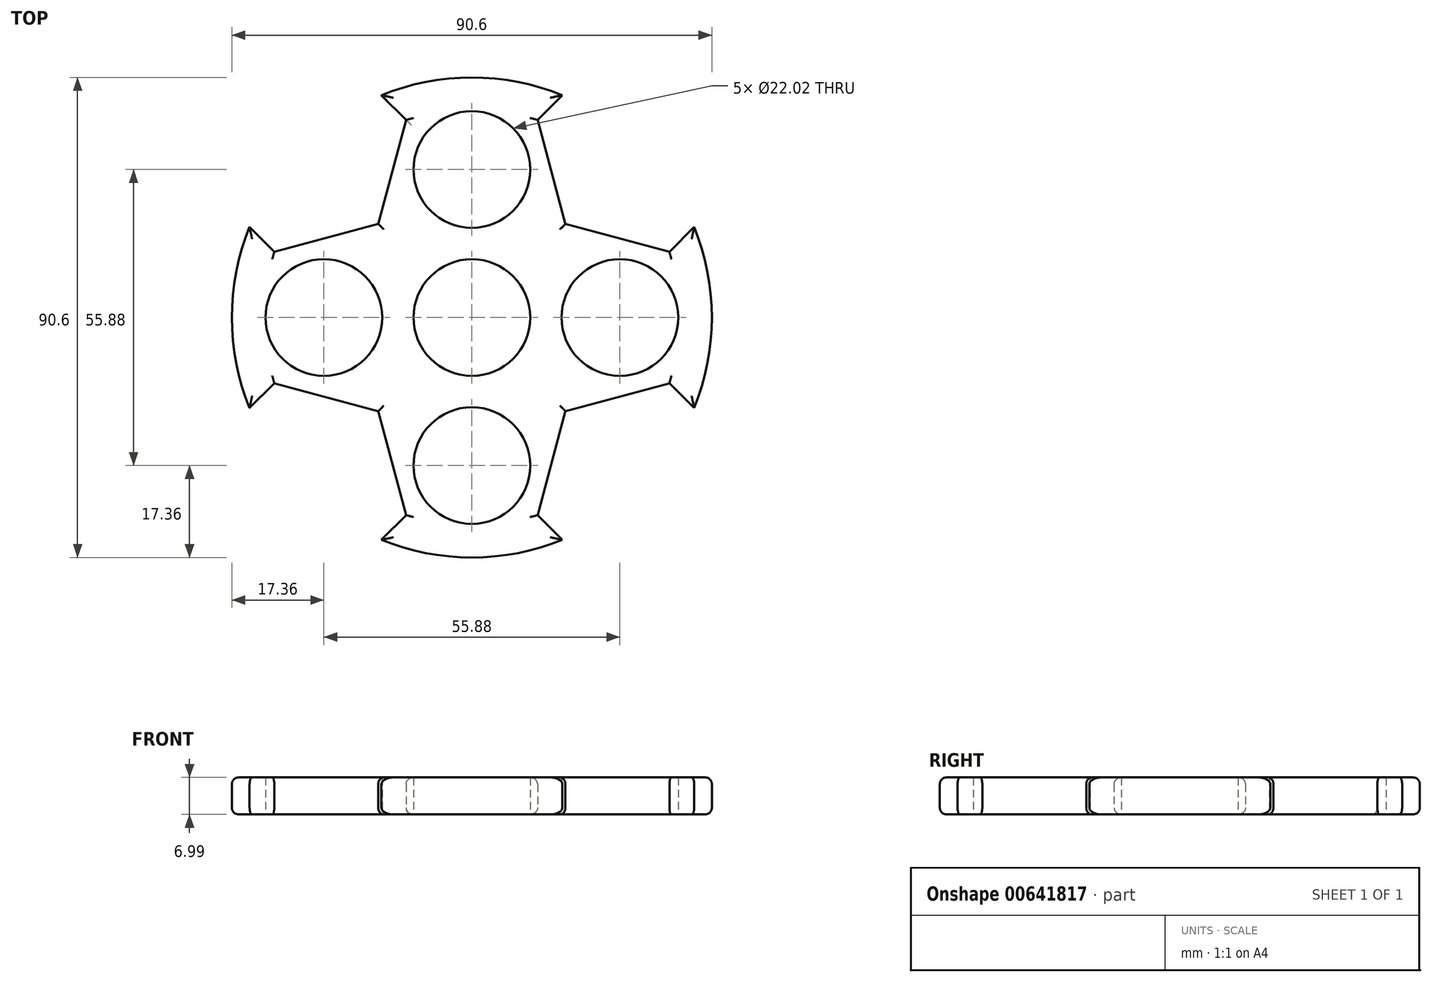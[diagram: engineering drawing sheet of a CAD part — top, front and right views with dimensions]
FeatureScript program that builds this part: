
annotation { "Feature Type Name" : "Feature", "Feature Type Description" : "" }
export const myFeature = defineFeature(function(context is Context, id is Id, definition is map)
    precondition{}
    {
        {
            var Q0;
            Q0=qCreatedBy(makeId("Top.planeOp"),FACE);
            var sketch = newSketch(context, id + "F0", { "sketchPlane" : qUnion([Q0])});
            skCircle(sketch, "E0", {"center": v(0, 0) * mm, "radius": 11.01 * mm});
            skCircle(sketch, "E1", {"center": v(0, 27.94) * mm, "radius": 11.01 * mm});
            skCircle(sketch, "E2", {"center": v(27.94, 0) * mm, "radius": 11.01 * mm});
            skLineSegment(sketch, "E3", {"start": v(0, 27.94) * mm, "end": v(0, 0) * mm});
            skLineSegment(sketch, "E4", {"start": v(27.94, 0) * mm, "end": v(0, 0) * mm});
            skCircle(sketch, "E5", {"center": v(0, -27.94) * mm, "radius": 11.01 * mm});
            skCircle(sketch, "E6", {"center": v(-27.94, 0) * mm, "radius": 11.01 * mm});
            skLineSegment(sketch, "E7", {"start": v(0, 0) * mm, "end": v(0, -27.94) * mm});
            skLineSegment(sketch, "E8", {"start": v(0, 0) * mm, "end": v(-27.94, 0) * mm});
            skCircle(sketch, "E9", {"center": v(0, 0) * mm, "radius": 45.3 * mm});
            skCircle(sketch, "E10.cCircle", {"center": v(-32.03, 32.03) * mm, "radius": 20.32 * mm, "construction": true});
            skLineSegment(sketch, "E10.0", {"start": v(-17.66, 17.66) * mm, "end": v(-37.3, 12.4) * mm});
            skLineSegment(sketch, "E10.1", {"start": v(-37.3, 12.4) * mm, "end": v(-51.66, 26.77) * mm});
            skLineSegment(sketch, "E10.2", {"start": v(-51.66, 26.77) * mm, "end": v(-46.4, 46.4) * mm});
            skLineSegment(sketch, "E10.3", {"start": v(-46.4, 46.4) * mm, "end": v(-26.77, 51.66) * mm});
            skLineSegment(sketch, "E10.4", {"start": v(-26.77, 51.66) * mm, "end": v(-12.4, 37.3) * mm});
            skLineSegment(sketch, "E10.5", {"start": v(-12.4, 37.3) * mm, "end": v(-17.66, 17.66) * mm});
            skLineSegment(sketch, "E11", {"start": v(0, 0) * mm, "end": v(-32.03, 32.03) * mm});
            skLineSegment(sketch, "E12.1.0", {"start": v(-26.77, -51.66) * mm, "end": v(-46.4, -46.4) * mm});
            skLineSegment(sketch, "E12.1.1", {"start": v(-17.66, -17.66) * mm, "end": v(-12.4, -37.3) * mm});
            skLineSegment(sketch, "E12.1.2", {"start": v(-46.4, -46.4) * mm, "end": v(-51.66, -26.77) * mm});
            skLineSegment(sketch, "E12.1.3", {"start": v(-51.66, -26.77) * mm, "end": v(-37.3, -12.4) * mm});
            skLineSegment(sketch, "E12.1.4", {"start": v(-37.3, -12.4) * mm, "end": v(-17.66, -17.66) * mm});
            skCircle(sketch, "E12.1.5", {"center": v(-32.03, -32.03) * mm, "radius": 20.32 * mm, "construction": true});
            skLineSegment(sketch, "E12.1.6", {"start": v(-12.4, -37.3) * mm, "end": v(-26.77, -51.66) * mm});
            skLineSegment(sketch, "E12.2.0", {"start": v(51.66, -26.77) * mm, "end": v(46.4, -46.4) * mm});
            skLineSegment(sketch, "E12.2.1", {"start": v(17.66, -17.66) * mm, "end": v(37.3, -12.4) * mm});
            skLineSegment(sketch, "E12.2.2", {"start": v(46.4, -46.4) * mm, "end": v(26.77, -51.66) * mm});
            skLineSegment(sketch, "E12.2.3", {"start": v(26.77, -51.66) * mm, "end": v(12.4, -37.3) * mm});
            skLineSegment(sketch, "E12.2.4", {"start": v(12.4, -37.3) * mm, "end": v(17.66, -17.66) * mm});
            skCircle(sketch, "E12.2.5", {"center": v(32.03, -32.03) * mm, "radius": 20.32 * mm, "construction": true});
            skLineSegment(sketch, "E12.2.6", {"start": v(37.3, -12.4) * mm, "end": v(51.66, -26.77) * mm});
            skLineSegment(sketch, "E12.3.0", {"start": v(26.77, 51.66) * mm, "end": v(46.4, 46.4) * mm});
            skLineSegment(sketch, "E12.3.1", {"start": v(17.66, 17.66) * mm, "end": v(12.4, 37.3) * mm});
            skLineSegment(sketch, "E12.3.2", {"start": v(46.4, 46.4) * mm, "end": v(51.66, 26.77) * mm});
            skLineSegment(sketch, "E12.3.3", {"start": v(51.66, 26.77) * mm, "end": v(37.3, 12.4) * mm});
            skLineSegment(sketch, "E12.3.4", {"start": v(37.3, 12.4) * mm, "end": v(17.66, 17.66) * mm});
            skCircle(sketch, "E12.3.5", {"center": v(32.03, 32.03) * mm, "radius": 20.32 * mm, "construction": true});
            skLineSegment(sketch, "E12.3.6", {"start": v(12.4, 37.3) * mm, "end": v(26.77, 51.66) * mm});
            skLineSegment(sketch, "E13", {"start": v(-32.03, -32.03) * mm, "end": v(0, 0) * mm});
            skLineSegment(sketch, "E14", {"start": v(0, 0) * mm, "end": v(32.03, -32.03) * mm});
            skLineSegment(sketch, "E15", {"start": v(0, 0) * mm, "end": v(32.03, 32.03) * mm});
            skSolve(sketch);
        }
        {
            var Q0;
            Q0=makeQuery(id+"F0.imprint","IMPRINT",FACE,{"disambiguationData":[TD([[makeQuery(id+"F0.imprint","IMPRINT",EDGE,{"derivedFrom":sQuery(id+"F0.wireOp",EDGE,"E2")}),-1.0]])]});
            var Q1;
            Q1=makeQuery(id+"F0.imprint","IMPRINT",FACE,{"disambiguationData":[TD([[makeQuery(id+"F0.imprint","IMPRINT",EDGE,{"derivedFrom":sQuery(id+"F0.wireOp",EDGE,"E1")}),-1.0]])]});
            var Q2;
            Q2=makeQuery(id+"F0.imprint","IMPRINT",FACE,{"disambiguationData":[TD([[makeQuery(id+"F0.imprint","IMPRINT",EDGE,{"derivedFrom":sQuery(id+"F0.wireOp",EDGE,"E6")}),-1.0]])]});
            var Q3;
            Q3=makeQuery(id+"F0.imprint","IMPRINT",FACE,{"disambiguationData":[TD([[makeQuery(id+"F0.imprint","IMPRINT",EDGE,{"derivedFrom":sQuery(id+"F0.wireOp",EDGE,"E5")}),-1.0]])]});
            extrude(context, id + "F1", {"entities" : qUnion([Q0, Q1, Q2, Q3]), "depth" : 7 * mm, "offsetDistance" : 25.4 * mm});
        }
        {
            var Q0;
            Q0=makeQuery(id+"F1.opExtrude","CAP_EDGE",EDGE,{"disambiguationData":[OSD([sQuery(id+"F0.wireOp",EDGE,"E10.5")])],"isStart":false});
            var Q1;
            Q1=makeQuery(id+"F1.opExtrude","CAP_EDGE",EDGE,{"disambiguationData":[OSD([sQuery(id+"F0.wireOp",EDGE,"E10.4")])],"isStart":false});
            var Q2;
            {var subQ0=sQuery(id+"F0.wireOp",EDGE,"E9");Q2=makeQuery(id+"F1.opExtrude","CAP_EDGE",EDGE,{"disambiguationData":[OSD([subQ0]),TDD([makeQuery(id+"F0.imprint","IMPRINT",EDGE,{"disambiguationData":[TD([[makeQuery(id+"F0.imprint","INTERSECT",VERTEX,{"derivedFrom":[subQ0,sQuery(id+"F0.wireOp",EDGE,"E12.3.6")]}),-1.0]])],"derivedFrom":subQ0})])],"isStart":false});}
            var Q3;
            Q3=makeQuery(id+"F1.opExtrude","CAP_EDGE",EDGE,{"disambiguationData":[OSD([sQuery(id+"F0.wireOp",EDGE,"E12.3.6")])],"isStart":false});
            var Q4;
            Q4=makeQuery(id+"F1.opExtrude","CAP_EDGE",EDGE,{"disambiguationData":[OSD([sQuery(id+"F0.wireOp",EDGE,"E12.3.1")])],"isStart":false});
            var Q5;
            Q5=makeQuery(id+"F1.opExtrude","CAP_EDGE",EDGE,{"disambiguationData":[OSD([sQuery(id+"F0.wireOp",EDGE,"E12.3.4")])],"isStart":false});
            var Q6;
            Q6=makeQuery(id+"F1.opExtrude","CAP_EDGE",EDGE,{"disambiguationData":[OSD([sQuery(id+"F0.wireOp",EDGE,"E10.0")])],"isStart":false});
            var Q7;
            Q7=makeQuery(id+"F1.opExtrude","CAP_EDGE",EDGE,{"disambiguationData":[OSD([sQuery(id+"F0.wireOp",EDGE,"E10.1")])],"isStart":false});
            var Q8;
            Q8=makeQuery(id+"F1.opExtrude","CAP_EDGE",EDGE,{"disambiguationData":[OSD([sQuery(id+"F0.wireOp",EDGE,"E12.1.3")])],"isStart":false});
            var Q9;
            Q9=makeQuery(id+"F1.opExtrude","CAP_EDGE",EDGE,{"disambiguationData":[OSD([sQuery(id+"F0.wireOp",EDGE,"E12.1.4")])],"isStart":false});
            var Q10;
            {var subQ0=sQuery(id+"F0.wireOp",EDGE,"E9");Q10=makeQuery(id+"F1.opExtrude","CAP_EDGE",EDGE,{"disambiguationData":[OSD([subQ0]),TDD([makeQuery(id+"F0.imprint","IMPRINT",EDGE,{"disambiguationData":[TD([[makeQuery(id+"F0.imprint","INTERSECT",VERTEX,{"derivedFrom":[subQ0,sQuery(id+"F0.wireOp",EDGE,"E10.1")]}),-1.0]])],"derivedFrom":subQ0})])],"isStart":false});}
            var Q11;
            Q11=makeQuery(id+"F1.opExtrude","CAP_EDGE",EDGE,{"disambiguationData":[OSD([sQuery(id+"F0.wireOp",EDGE,"E12.1.1")])],"isStart":false});
            var Q12;
            Q12=makeQuery(id+"F1.opExtrude","CAP_EDGE",EDGE,{"disambiguationData":[OSD([sQuery(id+"F0.wireOp",EDGE,"E12.1.6")])],"isStart":false});
            var Q13;
            {var subQ0=sQuery(id+"F0.wireOp",EDGE,"E9");Q13=makeQuery(id+"F1.opExtrude","CAP_EDGE",EDGE,{"disambiguationData":[OSD([subQ0]),TDD([makeQuery(id+"F0.imprint","IMPRINT",EDGE,{"disambiguationData":[TD([[makeQuery(id+"F0.imprint","INTERSECT",VERTEX,{"derivedFrom":[subQ0,sQuery(id+"F0.wireOp",EDGE,"E12.1.6")]}),-1.0]])],"derivedFrom":subQ0})])],"isStart":false});}
            var Q14;
            Q14=makeQuery(id+"F1.opExtrude","CAP_EDGE",EDGE,{"disambiguationData":[OSD([sQuery(id+"F0.wireOp",EDGE,"E12.2.3")])],"isStart":false});
            var Q15;
            Q15=makeQuery(id+"F1.opExtrude","CAP_EDGE",EDGE,{"disambiguationData":[OSD([sQuery(id+"F0.wireOp",EDGE,"E12.2.4")])],"isStart":false});
            var Q16;
            Q16=makeQuery(id+"F1.opExtrude","CAP_EDGE",EDGE,{"disambiguationData":[OSD([sQuery(id+"F0.wireOp",EDGE,"E12.2.1")])],"isStart":false});
            var Q17;
            Q17=makeQuery(id+"F1.opExtrude","CAP_EDGE",EDGE,{"disambiguationData":[OSD([sQuery(id+"F0.wireOp",EDGE,"E12.2.6")])],"isStart":false});
            var Q18;
            Q18=makeQuery(id+"F1.opExtrude","CAP_EDGE",EDGE,{"disambiguationData":[OSD([sQuery(id+"F0.wireOp",EDGE,"E12.3.3")])],"isStart":false});
            var Q19;
            {var subQ0=sQuery(id+"F0.wireOp",EDGE,"E9");Q19=makeQuery(id+"F1.opExtrude","CAP_EDGE",EDGE,{"disambiguationData":[OSD([subQ0]),TDD([makeQuery(id+"F0.imprint","IMPRINT",EDGE,{"disambiguationData":[TD([[makeQuery(id+"F0.imprint","INTERSECT",VERTEX,{"derivedFrom":[subQ0,sQuery(id+"F0.wireOp",EDGE,"E12.3.3")]}),1.0]])],"derivedFrom":subQ0})])],"isStart":false});}
            var Q20;
            {var subQ0=sQuery(id+"F0.wireOp",EDGE,"E9");Q20=makeQuery(id+"F1.opExtrude","CAP_EDGE",EDGE,{"disambiguationData":[OSD([subQ0]),TDD([makeQuery(id+"F0.imprint","IMPRINT",EDGE,{"disambiguationData":[TD([[makeQuery(id+"F0.imprint","INTERSECT",VERTEX,{"derivedFrom":[subQ0,sQuery(id+"F0.wireOp",EDGE,"E12.3.6")]}),-1.0]])],"derivedFrom":subQ0})])],"isStart":true});}
            var Q21;
            Q21=makeQuery(id+"F1.opExtrude","CAP_EDGE",EDGE,{"disambiguationData":[OSD([sQuery(id+"F0.wireOp",EDGE,"E10.5")])],"isStart":true});
            var Q22;
            Q22=makeQuery(id+"F1.opExtrude","CAP_EDGE",EDGE,{"disambiguationData":[OSD([sQuery(id+"F0.wireOp",EDGE,"E10.0")])],"isStart":true});
            var Q23;
            Q23=makeQuery(id+"F1.opExtrude","CAP_EDGE",EDGE,{"disambiguationData":[OSD([sQuery(id+"F0.wireOp",EDGE,"E10.1")])],"isStart":true});
            var Q24;
            {var subQ0=sQuery(id+"F0.wireOp",EDGE,"E9");Q24=makeQuery(id+"F1.opExtrude","CAP_EDGE",EDGE,{"disambiguationData":[OSD([subQ0]),TDD([makeQuery(id+"F0.imprint","IMPRINT",EDGE,{"disambiguationData":[TD([[makeQuery(id+"F0.imprint","INTERSECT",VERTEX,{"derivedFrom":[subQ0,sQuery(id+"F0.wireOp",EDGE,"E10.1")]}),-1.0]])],"derivedFrom":subQ0})])],"isStart":true});}
            var Q25;
            Q25=makeQuery(id+"F1.opExtrude","CAP_EDGE",EDGE,{"disambiguationData":[OSD([sQuery(id+"F0.wireOp",EDGE,"E12.1.4")])],"isStart":true});
            var Q26;
            Q26=makeQuery(id+"F1.opExtrude","CAP_EDGE",EDGE,{"disambiguationData":[OSD([sQuery(id+"F0.wireOp",EDGE,"E12.1.3")])],"isStart":true});
            var Q27;
            Q27=makeQuery(id+"F1.opExtrude","CAP_EDGE",EDGE,{"disambiguationData":[OSD([sQuery(id+"F0.wireOp",EDGE,"E12.1.1")])],"isStart":true});
            var Q28;
            Q28=makeQuery(id+"F1.opExtrude","CAP_EDGE",EDGE,{"disambiguationData":[OSD([sQuery(id+"F0.wireOp",EDGE,"E12.1.6")])],"isStart":true});
            var Q29;
            {var subQ0=sQuery(id+"F0.wireOp",EDGE,"E9");Q29=makeQuery(id+"F1.opExtrude","CAP_EDGE",EDGE,{"disambiguationData":[OSD([subQ0]),TDD([makeQuery(id+"F0.imprint","IMPRINT",EDGE,{"disambiguationData":[TD([[makeQuery(id+"F0.imprint","INTERSECT",VERTEX,{"derivedFrom":[subQ0,sQuery(id+"F0.wireOp",EDGE,"E12.1.6")]}),-1.0]])],"derivedFrom":subQ0})])],"isStart":true});}
            var Q30;
            Q30=makeQuery(id+"F1.opExtrude","CAP_EDGE",EDGE,{"disambiguationData":[OSD([sQuery(id+"F0.wireOp",EDGE,"E12.2.3")])],"isStart":true});
            var Q31;
            Q31=makeQuery(id+"F1.opExtrude","CAP_EDGE",EDGE,{"disambiguationData":[OSD([sQuery(id+"F0.wireOp",EDGE,"E12.2.4")])],"isStart":true});
            var Q32;
            Q32=makeQuery(id+"F1.opExtrude","CAP_EDGE",EDGE,{"disambiguationData":[OSD([sQuery(id+"F0.wireOp",EDGE,"E12.2.1")])],"isStart":true});
            var Q33;
            Q33=makeQuery(id+"F1.opExtrude","CAP_EDGE",EDGE,{"disambiguationData":[OSD([sQuery(id+"F0.wireOp",EDGE,"E12.2.6")])],"isStart":true});
            var Q34;
            {var subQ0=sQuery(id+"F0.wireOp",EDGE,"E9");Q34=makeQuery(id+"F1.opExtrude","CAP_EDGE",EDGE,{"disambiguationData":[OSD([subQ0]),TDD([makeQuery(id+"F0.imprint","IMPRINT",EDGE,{"disambiguationData":[TD([[makeQuery(id+"F0.imprint","INTERSECT",VERTEX,{"derivedFrom":[subQ0,sQuery(id+"F0.wireOp",EDGE,"E12.3.3")]}),1.0]])],"derivedFrom":subQ0})])],"isStart":true});}
            var Q35;
            Q35=makeQuery(id+"F1.opExtrude","CAP_EDGE",EDGE,{"disambiguationData":[OSD([sQuery(id+"F0.wireOp",EDGE,"E12.3.4")])],"isStart":true});
            var Q36;
            Q36=makeQuery(id+"F1.opExtrude","CAP_EDGE",EDGE,{"disambiguationData":[OSD([sQuery(id+"F0.wireOp",EDGE,"E12.3.3")])],"isStart":true});
            var Q37;
            Q37=makeQuery(id+"F1.opExtrude","CAP_EDGE",EDGE,{"disambiguationData":[OSD([sQuery(id+"F0.wireOp",EDGE,"E12.3.1")])],"isStart":true});
            var Q38;
            Q38=makeQuery(id+"F1.opExtrude","CAP_EDGE",EDGE,{"disambiguationData":[OSD([sQuery(id+"F0.wireOp",EDGE,"E12.3.6")])],"isStart":true});
            fillet(context, id + "F2", {"entities" : qUnion([Q0, Q1, Q2, Q3, Q4, Q5, Q6, Q7, Q8, Q9, Q10, Q11, Q12, Q13, Q14, Q15, Q16, Q17, Q18, Q19, Q20, Q21, Q22, Q23, Q24, Q25, Q26, Q27, Q28, Q29, Q30, Q31, Q32, Q33, Q34, Q35, Q36, Q37, Q38]), "radius" : 1.27 * mm, "tangentPropagation" : true, "allowEdgeOverflow" : false});
        }
    });
